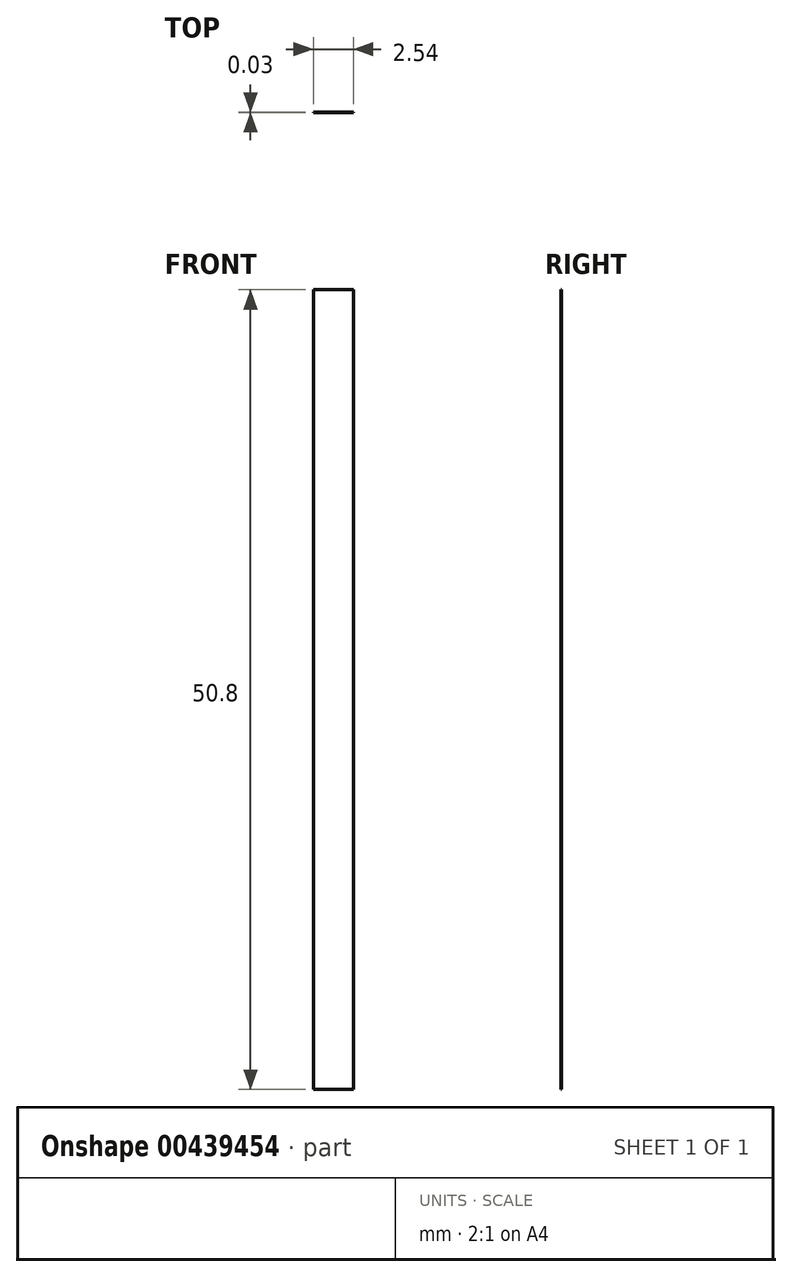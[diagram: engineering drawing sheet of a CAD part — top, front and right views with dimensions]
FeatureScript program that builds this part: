
annotation { "Feature Type Name" : "Feature", "Feature Type Description" : "" }
export const myFeature = defineFeature(function(context is Context, id is Id, definition is map)
    precondition{}
    {
        {
            var Q0;
            Q0=qCreatedBy(makeId("Front.planeOp"),FACE);
            var sketch = newSketch(context, id + "F0", { "sketchPlane" : qUnion([Q0])});
            skLineSegment(sketch, "E0.bottom", {"start": v(0, 21.64) * mm, "end": v(-2.54, 21.64) * mm});
            skLineSegment(sketch, "E0.top", {"start": v(0, -29.16) * mm, "end": v(-2.54, -29.16) * mm});
            skLineSegment(sketch, "E0.left", {"start": v(0, 21.64) * mm, "end": v(0, -29.16) * mm});
            skLineSegment(sketch, "E0.right", {"start": v(-2.54, 21.64) * mm, "end": v(-2.54, -29.16) * mm});
            skSolve(sketch);
        }
        {
            var Q0;
            Q0=makeQuery(id+"F0.imprint","IMPRINT",FACE,{"disambiguationData":[TD([[makeQuery(id+"F0.imprint","IMPRINT",EDGE,{"derivedFrom":sQuery(id+"F0.wireOp",EDGE,"E0.bottom")}),1.0]])]});
            extrude(context, id + "F1", {"entities" : qUnion([Q0]), "depth" : 0.03 * mm});
        }
    });
